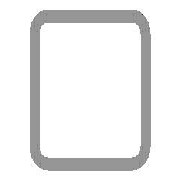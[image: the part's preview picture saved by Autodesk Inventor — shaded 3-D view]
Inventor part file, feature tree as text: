
AUTODESK INVENTOR PART (.ipt)
format: ipt  version: 2025 (Build 290162010, 162A)  size: 135,680 bytes
history: native  units: mm (DEFAULTED — no unit token found)
features: other x4, sketch x1, plane x1
ambient origin geometry x8: Origin, YZ Plane, XZ Plane, XY Plane, X Axis, Y Axis, Z Axis, Center Point
bodies: Solid1 (feature_tree), Body (feature_tree)
feature tree (6):
  parser-record x1  (decoder bookkeeping rows leaked as tree rows — omitted from the tree; the rows remain in map.json)
  other  "Driven Length"
  other  "Start Plane"
  other  "End Plane"
  sketch  "Sketch3"  dims[d3=2025.0mm d4=0.0mm d7=4.5mm d10=80.0mm d11=80.0mm d12=3.0mm d13=-0.0mm d14=2025.0mm d15=40.0mm d16=40.0mm d17=90.0deg d18=2025.0mm]
  plane  "Work Plane3"
